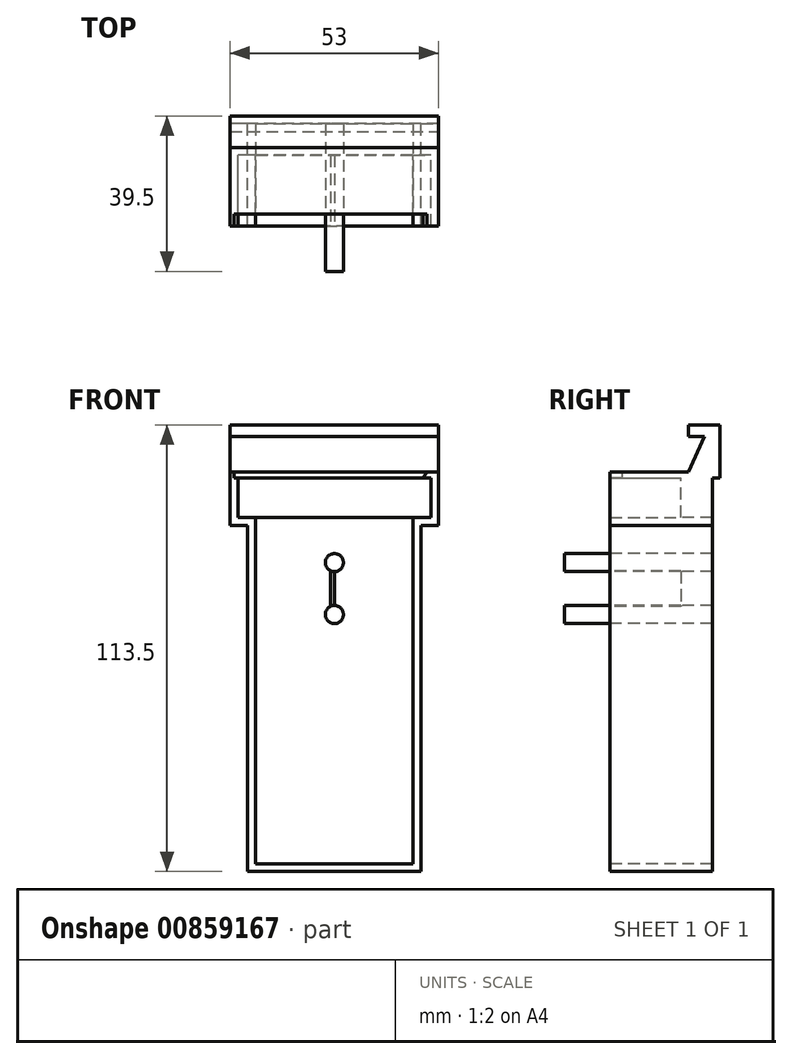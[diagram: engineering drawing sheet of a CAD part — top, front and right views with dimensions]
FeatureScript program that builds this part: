
annotation { "Feature Type Name" : "Feature", "Feature Type Description" : "" }
export const myFeature = defineFeature(function(context is Context, id is Id, definition is map)
    precondition{}
    {
        {
            var Q0;
            Q0=qCreatedBy(makeId("Front.planeOp"),FACE);
            var sketch = newSketch(context, id + "F0", { "sketchPlane" : qUnion([Q0])});
            skLineSegment(sketch, "E0.bottom", {"start": v(0, 0) * mm, "end": v(53, 0) * mm});
            skLineSegment(sketch, "E0.top", {"start": v(0, 3) * mm, "end": v(53, 3) * mm});
            skLineSegment(sketch, "E0.left", {"start": v(0, 0) * mm, "end": v(0, 3) * mm});
            skLineSegment(sketch, "E0.right", {"start": v(53, 0) * mm, "end": v(53, 3) * mm});
            skSolve(sketch);
        }
        {
            var Q0;
            Q0 = qSketchRegion(id + "F0", true);
            extrude(context, id + "F1", {"entities" : qUnion([Q0]), "depth" : 8 * mm, "offsetDistance" : 25 * mm});
        }
        {
            var Q0;
            Q0=makeQuery(id+"F1.opExtrude","SWEPT_FACE",FACE,{"disambiguationData":[OSD([sQuery(id+"F0.wireOp",EDGE,"E0.right")])]});
            var sketch = newSketch(context, id + "F2", { "sketchPlane" : qUnion([Q0])});
            skLineSegment(sketch, "E1", {"start": v(0, 0) * mm, "end": v(-4, 0) * mm});
            skLineSegment(sketch, "E2", {"start": v(0, 0) * mm, "end": v(0, -9) * mm});
            skLineSegment(sketch, "E3", {"start": v(0, -9) * mm, "end": v(-8, -9) * mm});
            skLineSegment(sketch, "E4", {"start": v(-8, -9) * mm, "end": v(-4, 0) * mm});
            skSolve(sketch);
        }
        {
            var Q0;
            Q0 = qSketchRegion(id + "F2", true);
            extrude(context, id + "F3", {"entities" : qUnion([Q0]), "operationType" : NewBodyOperationType.ADD, "depth" : -53 * mm, "offsetDistance" : 25 * mm});
        }
        {
            var Q0;
            Q0=makeQuery(id+"F1.opExtrude","CAP_FACE",FACE,{"disambiguationData":[OSD([sQuery(id+"F0.wireOp",EDGE,"E0.bottom"),sQuery(id+"F0.wireOp",EDGE,"E0.top"),sQuery(id+"F0.wireOp",EDGE,"E0.left"),sQuery(id+"F0.wireOp",EDGE,"E0.right")])],"isStart":false});
            var sketch = newSketch(context, id + "F4", { "sketchPlane" : qUnion([Q0])});
            skLineSegment(sketch, "E5", {"start": v(53, 3) * mm, "end": v(53, -9) * mm});
            skPoint(sketch, "E5.endSnap0", {"position": v(53, 1.5) * mm});
            skLineSegment(sketch, "E6.bottom", {"start": v(53, -9) * mm, "end": v(50, -9) * mm});
            skLineSegment(sketch, "E6.left", {"start": v(53, -9) * mm, "end": v(53, -10) * mm});
            skLineSegment(sketch, "E7", {"start": v(49.5, -9) * mm, "end": v(50, -9) * mm});
            skLineSegment(sketch, "E8", {"start": v(49.5, -9) * mm, "end": v(45, -9) * mm});
            skLineSegment(sketch, "E9", {"start": v(45, -9) * mm, "end": v(45, -10) * mm});
            skLineSegment(sketch, "E10", {"start": v(53, -9) * mm, "end": v(53, -10.5) * mm});
            skLineSegment(sketch, "E11", {"start": v(53, -10.5) * mm, "end": v(50, -10.5) * mm});
            skLineSegment(sketch, "E12", {"start": v(45, -10) * mm, "end": v(45, -10.5) * mm});
            skLineSegment(sketch, "E13", {"start": v(45, -10.5) * mm, "end": v(50, -10.5) * mm});
            skLineSegment(sketch, "E14", {"start": v(53, -10.5) * mm, "end": v(49, -10.5) * mm});
            skLineSegment(sketch, "E15", {"start": v(49, -10.5) * mm, "end": v(50, -9) * mm});
            skLineSegment(sketch, "E16", {"start": v(49.5, -9) * mm, "end": v(49.5, -9.75) * mm});
            skSolve(sketch);
        }
        {
            var Q0;
            Q0=makeQuery(id+"F4.imprint","IMPRINT",FACE,{"disambiguationData":[TD([[makeQuery(id+"F4.imprint","IMPRINT",EDGE,{"derivedFrom":sQuery(id+"F4.wireOp",EDGE,"t7llfW6A-werJ-ecjy-mYfy-ns4PyMyV4q1R")}),1.0]])]});
            var Q1;
            Q1=makeQuery(id+"F4.imprint","IMPRINT",FACE,{"disambiguationData":[TD([[makeQuery(id+"F4.imprint","IMPRINT",EDGE,{"derivedFrom":sQuery(id+"F4.wireOp",EDGE,"E6.right")}),-1.0]])]});
            var Q2;
            Q2=makeQuery(id+"F4.imprint","IMPRINT",FACE,{"disambiguationData":[TD([[makeQuery(id+"F4.imprint","IMPRINT",EDGE,{"derivedFrom":sQuery(id+"F4.wireOp",EDGE,"E6.bottom")}),1.0]])]});
            extrude(context, id + "F5", {"entities" : qUnion([Q0, Q1, Q2]), "operationType" : NewBodyOperationType.ADD, "depth" : -8 * mm, "offsetDistance" : 25 * mm});
        }
        {
            var Q0;
            Q0=makeQuery(id+"F4.imprint","IMPRINT",FACE,{"disambiguationData":[TD([[makeQuery(id+"F4.imprint","IMPRINT",EDGE,{"derivedFrom":sQuery(id+"F4.wireOp",EDGE,"E6.bottom")}),1.0]])]});
            var Q1;
            Q1=makeQuery(id+"F4.imprint","IMPRINT",FACE,{"disambiguationData":[TD([[makeQuery(id+"F4.imprint","IMPRINT",EDGE,{"derivedFrom":sQuery(id+"F4.wireOp",EDGE,"E6.right")}),-1.0]])]});
            var Q2;
            Q2=makeQuery(id+"F4.imprint","IMPRINT",FACE,{"disambiguationData":[TD([[makeQuery(id+"F4.imprint","IMPRINT",EDGE,{"derivedFrom":sQuery(id+"F4.wireOp",EDGE,"t7llfW6A-werJ-ecjy-mYfy-ns4PyMyV4q1R")}),1.0]])]});
            extrude(context, id + "F6", {"entities" : qUnion([Q0, Q1, Q2]), "operationType" : NewBodyOperationType.ADD, "depth" : 17 * mm, "offsetDistance" : 25 * mm});
        }
        {
            var Q0;
            Q0=makeQuery(id+"F4.imprint","IMPRINT",FACE,{"disambiguationData":[TD([[makeQuery(id+"F4.imprint","IMPRINT",EDGE,{"derivedFrom":sQuery(id+"F4.wireOp",EDGE,"E6.right")}),-1.0]])]});
            var Q1;
            Q1=makeQuery(id+"F4.imprint","IMPRINT",FACE,{"disambiguationData":[TD([[makeQuery(id+"F4.imprint","IMPRINT",EDGE,{"derivedFrom":sQuery(id+"F4.wireOp",EDGE,"E6.bottom")}),1.0]])]});
            extrude(context, id + "F7", {"entities" : qUnion([Q0, Q1]), "operationType" : NewBodyOperationType.ADD, "depth" : 20 * mm, "offsetDistance" : 25 * mm});
        }
        {
            var Q0;
            Q0=makeQuery(id+"F1.opExtrude","CAP_FACE",FACE,{"disambiguationData":[OSD([sQuery(id+"F0.wireOp",EDGE,"E0.bottom"),sQuery(id+"F0.wireOp",EDGE,"E0.top"),sQuery(id+"F0.wireOp",EDGE,"E0.left"),sQuery(id+"F0.wireOp",EDGE,"E0.right")])],"isStart":false});
            var sketch = newSketch(context, id + "F8", { "sketchPlane" : qUnion([Q0])});
            skLineSegment(sketch, "E17", {"start": v(0, 3) * mm, "end": v(0, -9) * mm});
            skLineSegment(sketch, "E18.bottom", {"start": v(0, -9) * mm, "end": v(1, -9) * mm});
            skLineSegment(sketch, "E18.top", {"start": v(0, -10.5) * mm, "end": v(1, -10.5) * mm});
            skLineSegment(sketch, "E18.left", {"start": v(0, -9) * mm, "end": v(0, -10.5) * mm});
            skLineSegment(sketch, "E18.right", {"start": v(1, -9) * mm, "end": v(1, -10.5) * mm});
            skLineSegment(sketch, "E19.bottom", {"start": v(1, -10.5) * mm, "end": v(8, -10.5) * mm});
            skLineSegment(sketch, "E19.top", {"start": v(1, -9) * mm, "end": v(8, -9) * mm});
            skLineSegment(sketch, "E19.left", {"start": v(1, -10.5) * mm, "end": v(1, -9) * mm});
            skLineSegment(sketch, "E20", {"start": v(8, -9) * mm, "end": v(49.5, -9) * mm});
            skLineSegment(sketch, "E21", {"start": v(8, -10.5) * mm, "end": v(49.5, -10.5) * mm});
            skLineSegment(sketch, "E22", {"start": v(49.5, -10.5) * mm, "end": v(49.5, -9) * mm});
            skSolve(sketch);
        }
        {
            var Q0;
            Q0=makeQuery(id+"F8.imprint","IMPRINT",FACE,{"disambiguationData":[TD([[makeQuery(id+"F8.imprint","IMPRINT",EDGE,{"derivedFrom":sQuery(id+"F8.wireOp",EDGE,"E18.bottom")}),-1.0]])]});
            var Q1;
            Q1=makeQuery(id+"F8.imprint","IMPRINT",FACE,{"disambiguationData":[TD([[makeQuery(id+"F8.imprint","IMPRINT",EDGE,{"derivedFrom":sQuery(id+"F8.wireOp",EDGE,"E19.bottom")}),1.0]])]});
            extrude(context, id + "F9", {"entities" : qUnion([Q0, Q1]), "operationType" : NewBodyOperationType.ADD, "depth" : -8 * mm, "offsetDistance" : 25 * mm});
        }
        {
            var Q0;
            Q0=makeQuery(id+"F8.imprint","IMPRINT",FACE,{"disambiguationData":[TD([[makeQuery(id+"F8.imprint","IMPRINT",EDGE,{"derivedFrom":sQuery(id+"F8.wireOp",EDGE,"E18.bottom")}),-1.0]])]});
            extrude(context, id + "F10", {"entities" : qUnion([Q0]), "operationType" : NewBodyOperationType.ADD, "depth" : 20 * mm, "offsetDistance" : 25 * mm});
        }
        {
            var Q0;
            Q0=makeQuery(id+"F8.imprint","IMPRINT",FACE,{"disambiguationData":[TD([[makeQuery(id+"F8.imprint","IMPRINT",EDGE,{"derivedFrom":sQuery(id+"F8.wireOp",EDGE,"E19.bottom")}),1.0]])]});
            extrude(context, id + "F11", {"entities" : qUnion([Q0]), "operationType" : NewBodyOperationType.ADD, "depth" : 17 * mm, "offsetDistance" : 25 * mm});
        }
        {
            var Q0;
            {var subQ0=sQuery(id+"F8.wireOp",EDGE,"E21");var subQ1=sQuery(id+"F8.wireOp",EDGE,"E19.bottom");var subQ2=sQuery(id+"F8.wireOp",EDGE,"E18.top");var subQ3=sQuery(id+"F4.wireOp",EDGE,"E13");var subQ4=sQuery(id+"F4.wireOp",EDGE,"E11");Q0=makeQuery(id+"F11.boolean.opBoolean","MERGE",FACE,{"derivedFrom":[makeQuery(id+"F10.boolean.opBoolean","MERGE",FACE,{"derivedFrom":[makeQuery(id+"F9.boolean.opBoolean","MERGE",FACE,{"derivedFrom":[makeQuery(id+"F7.boolean.opBoolean","MERGE",FACE,{"derivedFrom":[makeQuery(id+"F6.boolean.opBoolean","MERGE",FACE,{"derivedFrom":[makeQuery(id+"F5.opExtrude","SWEPT_FACE",FACE,{"disambiguationData":[OSD([subQ4,subQ3])]}),makeQuery(id+"F6.opExtrude","SWEPT_FACE",FACE,{"disambiguationData":[OSD([subQ4,subQ3])]})]}),makeQuery(id+"F7.opExtrude","SWEPT_FACE",FACE,{"disambiguationData":[OSD([subQ4,subQ3])]})]}),makeQuery(id+"F9.opExtrude","SWEPT_FACE",FACE,{"disambiguationData":[OSD([subQ2,subQ1,subQ0])]})]}),makeQuery(id+"F10.opExtrude","SWEPT_FACE",FACE,{"disambiguationData":[OSD([subQ2])]})]}),makeQuery(id+"F11.opExtrude","SWEPT_FACE",FACE,{"disambiguationData":[OSD([subQ1,subQ0])]})]});}
            var sketch = newSketch(context, id + "F12", { "sketchPlane" : qUnion([Q0])});
            skLineSegment(sketch, "E23.bottom", {"start": v(53, 28) * mm, "end": v(51, 28) * mm});
            skLineSegment(sketch, "E23.top", {"start": v(53, 15) * mm, "end": v(51, 15) * mm});
            skLineSegment(sketch, "E23.left", {"start": v(53, 28) * mm, "end": v(53, 15) * mm});
            skLineSegment(sketch, "E23.right", {"start": v(51, 28) * mm, "end": v(51, 15) * mm});
            skSolve(sketch);
        }
        {
            var Q0;
            Q0 = qSketchRegion(id + "F12", true);
            extrude(context, id + "F13", {"entities" : qUnion([Q0]), "operationType" : NewBodyOperationType.ADD, "depth" : 12 * mm, "offsetDistance" : 25 * mm});
        }
        {
            var Q0;
            Q0=makeQuery(id+"F13.opExtrude","SWEPT_FACE",FACE,{"disambiguationData":[OSD([sQuery(id+"F12.wireOp",EDGE,"E23.right")])]});
            var sketch = newSketch(context, id + "F14", { "sketchPlane" : qUnion([Q0])});
            skLineSegment(sketch, "E24.bottom", {"start": v(28, -22.5) * mm, "end": v(10, -22.5) * mm});
            skLineSegment(sketch, "E24.top", {"start": v(28, -20.5) * mm, "end": v(10, -20.5) * mm});
            skLineSegment(sketch, "E24.left", {"start": v(28, -22.5) * mm, "end": v(28, -20.5) * mm});
            skLineSegment(sketch, "E24.right", {"start": v(10, -22.5) * mm, "end": v(10, -20.5) * mm});
            skSolve(sketch);
        }
        {
            var Q0;
            Q0 = qSketchRegion(id + "F14", true);
            extrude(context, id + "F15", {"entities" : qUnion([Q0]), "operationType" : NewBodyOperationType.ADD, "depth" : 2.5 * mm, "offsetDistance" : 25 * mm});
        }
        {
            var Q0;
            {var subQ0=sQuery(id+"F4.wireOp",EDGE,"E7");Q0=makeQuery(id+"F4.imprint","IMPRINT",FACE,{"disambiguationData":[TD([[makeQuery(id+"F4.imprint","IMPRINT",EDGE,{"derivedFrom":subQ0}),-1.0]])]});}
            extrude(context, id + "F16", {"entities" : qUnion([Q0]), "operationType" : NewBodyOperationType.ADD, "depth" : -8 * mm, "offsetDistance" : 25 * mm});
        }
        {
            var Q0;
            {var subQ0=sQuery(id+"F4.wireOp",EDGE,"E7");Q0=makeQuery(id+"F4.imprint","IMPRINT",FACE,{"disambiguationData":[TD([[makeQuery(id+"F4.imprint","IMPRINT",EDGE,{"derivedFrom":subQ0}),-1.0]])]});}
            extrude(context, id + "F17", {"entities" : qUnion([Q0]), "operationType" : NewBodyOperationType.ADD, "depth" : 17 * mm, "offsetDistance" : 25 * mm});
        }
        {
            var Q0;
            Q0=makeQuery(id+"F15.boolean.opBoolean","MERGE",FACE,{"derivedFrom":[makeQuery(id+"F13.opExtrude","CAP_FACE",FACE,{"disambiguationData":[OSD([sQuery(id+"F12.wireOp",EDGE,"E23.bottom"),sQuery(id+"F12.wireOp",EDGE,"E23.top"),sQuery(id+"F12.wireOp",EDGE,"E23.left"),sQuery(id+"F12.wireOp",EDGE,"E23.right")])],"isStart":false}),makeQuery(id+"F15.opExtrude","SWEPT_FACE",FACE,{"disambiguationData":[OSD([sQuery(id+"F14.wireOp",EDGE,"E24.bottom")])]})]});
            var sketch = newSketch(context, id + "F18", { "sketchPlane" : qUnion([Q0])});
            skLineSegment(sketch, "E25.bottom", {"start": v(48.5, 28) * mm, "end": v(46.5, 28) * mm});
            skLineSegment(sketch, "E25.top", {"start": v(48.5, 10) * mm, "end": v(46.5, 10) * mm});
            skLineSegment(sketch, "E25.left", {"start": v(48.5, 28) * mm, "end": v(48.5, 10) * mm});
            skLineSegment(sketch, "E25.right", {"start": v(46.5, 28) * mm, "end": v(46.5, 10) * mm});
            skSolve(sketch);
        }
        {
            var Q0;
            Q0 = qSketchRegion(id + "F18", true);
            extrude(context, id + "F19", {"entities" : qUnion([Q0]), "operationType" : NewBodyOperationType.ADD, "depth" : -2 * mm, "offsetDistance" : 25 * mm});
        }
        {
            var Q0;
            Q0 = qSketchRegion(id + "F18", true);
            extrude(context, id + "F20", {"entities" : qUnion([Q0]), "operationType" : NewBodyOperationType.ADD, "depth" : 88 * mm, "offsetDistance" : 25 * mm});
        }
        {
            var Q0;
            {var subQ0=sQuery(id+"F8.wireOp",EDGE,"E21");var subQ1=sQuery(id+"F8.wireOp",EDGE,"E19.bottom");var subQ2=sQuery(id+"F8.wireOp",EDGE,"E18.top");var subQ3=sQuery(id+"F4.wireOp",EDGE,"E14");Q0=makeQuery(id+"F11.boolean.opBoolean","MERGE",FACE,{"derivedFrom":[makeQuery(id+"F10.boolean.opBoolean","MERGE",FACE,{"derivedFrom":[makeQuery(id+"F9.boolean.opBoolean","MERGE",FACE,{"derivedFrom":[makeQuery(id+"F7.boolean.opBoolean","MERGE",FACE,{"derivedFrom":[makeQuery(id+"F6.boolean.opBoolean","MERGE",FACE,{"derivedFrom":[makeQuery(id+"F5.opExtrude","SWEPT_FACE",FACE,{"disambiguationData":[OSD([subQ3])]}),makeQuery(id+"F6.opExtrude","SWEPT_FACE",FACE,{"disambiguationData":[OSD([subQ3])]})]}),makeQuery(id+"F7.opExtrude","SWEPT_FACE",FACE,{"disambiguationData":[OSD([subQ3])]})]}),makeQuery(id+"F9.opExtrude","SWEPT_FACE",FACE,{"disambiguationData":[OSD([subQ2,subQ1,subQ0])]})]}),makeQuery(id+"F10.opExtrude","SWEPT_FACE",FACE,{"disambiguationData":[OSD([subQ2])]})]}),makeQuery(id+"F11.opExtrude","SWEPT_FACE",FACE,{"disambiguationData":[OSD([subQ1,subQ0])]})]});}
            var sketch = newSketch(context, id + "F21", { "sketchPlane" : qUnion([Q0])});
            skLineSegment(sketch, "E26.bottom", {"start": v(0, 28) * mm, "end": v(2, 28) * mm});
            skLineSegment(sketch, "E26.top", {"start": v(0, 15) * mm, "end": v(2, 15) * mm});
            skLineSegment(sketch, "E26.left", {"start": v(0, 28) * mm, "end": v(0, 15) * mm});
            skLineSegment(sketch, "E26.right", {"start": v(2, 28) * mm, "end": v(2, 15) * mm});
            skSolve(sketch);
        }
        {
            var Q0;
            Q0 = qSketchRegion(id + "F21", true);
            extrude(context, id + "F22", {"entities" : qUnion([Q0]), "operationType" : NewBodyOperationType.ADD, "depth" : 12 * mm, "offsetDistance" : 25 * mm});
        }
        {
            var Q0;
            Q0=makeQuery(id+"F22.opExtrude","SWEPT_FACE",FACE,{"disambiguationData":[OSD([sQuery(id+"F21.wireOp",EDGE,"E26.right")])]});
            var sketch = newSketch(context, id + "F23", { "sketchPlane" : qUnion([Q0])});
            skLineSegment(sketch, "E27.bottom", {"start": v(-28, -22.5) * mm, "end": v(-10, -22.5) * mm});
            skLineSegment(sketch, "E27.top", {"start": v(-28, -20.5) * mm, "end": v(-10, -20.5) * mm});
            skLineSegment(sketch, "E27.left", {"start": v(-28, -22.5) * mm, "end": v(-28, -20.5) * mm});
            skLineSegment(sketch, "E27.right", {"start": v(-10, -22.5) * mm, "end": v(-10, -20.5) * mm});
            skSolve(sketch);
        }
        {
            var Q0;
            Q0 = qSketchRegion(id + "F23", true);
            extrude(context, id + "F24", {"entities" : qUnion([Q0]), "operationType" : NewBodyOperationType.ADD, "depth" : 4.5 * mm, "offsetDistance" : 25 * mm});
        }
        {
            var Q0;
            Q0=makeQuery(id+"F24.boolean.opBoolean","MERGE",FACE,{"derivedFrom":[makeQuery(id+"F22.opExtrude","CAP_FACE",FACE,{"disambiguationData":[OSD([sQuery(id+"F21.wireOp",EDGE,"E26.bottom"),sQuery(id+"F21.wireOp",EDGE,"E26.top"),sQuery(id+"F21.wireOp",EDGE,"E26.left"),sQuery(id+"F21.wireOp",EDGE,"E26.right")])],"isStart":false}),makeQuery(id+"F24.opExtrude","SWEPT_FACE",FACE,{"disambiguationData":[OSD([sQuery(id+"F23.wireOp",EDGE,"E27.bottom")])]})]});
            var sketch = newSketch(context, id + "F25", { "sketchPlane" : qUnion([Q0])});
            skLineSegment(sketch, "E28.bottom", {"start": v(6.5, 28) * mm, "end": v(4.5, 28) * mm});
            skLineSegment(sketch, "E28.top", {"start": v(6.5, 10) * mm, "end": v(4.5, 10) * mm});
            skLineSegment(sketch, "E28.left", {"start": v(6.5, 28) * mm, "end": v(6.5, 10) * mm});
            skLineSegment(sketch, "E28.right", {"start": v(4.5, 28) * mm, "end": v(4.5, 10) * mm});
            skSolve(sketch);
        }
        {
            var Q0;
            Q0 = qSketchRegion(id + "F25", true);
            extrude(context, id + "F26", {"entities" : qUnion([Q0]), "operationType" : NewBodyOperationType.ADD, "depth" : 88 * mm, "offsetDistance" : 25 * mm});
        }
        {
            var Q0;
            Q0=makeQuery(id+"F22.opExtrude","SWEPT_FACE",FACE,{"disambiguationData":[OSD([sQuery(id+"F21.wireOp",EDGE,"E26.top")])]});
            var sketch = newSketch(context, id + "F27", { "sketchPlane" : qUnion([Q0])});
            skLineSegment(sketch, "E29.bottom", {"start": v(0, -10.5) * mm, "end": v(-2, -10.5) * mm});
            skLineSegment(sketch, "E29.top", {"start": v(0, -22.5) * mm, "end": v(-2, -22.5) * mm});
            skLineSegment(sketch, "E29.left", {"start": v(0, -10.5) * mm, "end": v(0, -22.5) * mm});
            skLineSegment(sketch, "E29.right", {"start": v(-2, -10.5) * mm, "end": v(-2, -22.5) * mm});
            skSolve(sketch);
        }
        {
            var Q0;
            Q0 = qSketchRegion(id + "F27", true);
            extrude(context, id + "F28", {"entities" : qUnion([Q0]), "operationType" : NewBodyOperationType.ADD, "depth" : 5 * mm, "offsetDistance" : 25 * mm});
        }
        {
            var Q0;
            Q0=makeQuery(id+"F13.opExtrude","SWEPT_FACE",FACE,{"disambiguationData":[OSD([sQuery(id+"F12.wireOp",EDGE,"E23.top")])]});
            var sketch = newSketch(context, id + "F29", { "sketchPlane" : qUnion([Q0])});
            skLineSegment(sketch, "E30.bottom", {"start": v(-51, -10.5) * mm, "end": v(-53, -10.5) * mm});
            skLineSegment(sketch, "E30.top", {"start": v(-51, -22.5) * mm, "end": v(-53, -22.5) * mm});
            skLineSegment(sketch, "E30.left", {"start": v(-51, -10.5) * mm, "end": v(-51, -22.5) * mm});
            skLineSegment(sketch, "E30.right", {"start": v(-53, -10.5) * mm, "end": v(-53, -22.5) * mm});
            skSolve(sketch);
        }
        {
            var Q0;
            Q0 = qSketchRegion(id + "F29", true);
            extrude(context, id + "F30", {"entities" : qUnion([Q0]), "operationType" : NewBodyOperationType.ADD, "depth" : 5 * mm, "offsetDistance" : 25 * mm});
        }
        {
            var Q0;
            Q0=makeQuery(id+"F28.boolean.opBoolean","MERGE",FACE,{"derivedFrom":[makeQuery(id+"F26.boolean.opBoolean","MERGE",FACE,{"derivedFrom":[makeQuery(id+"F24.opExtrude","SWEPT_FACE",FACE,{"disambiguationData":[OSD([sQuery(id+"F23.wireOp",EDGE,"E27.right")])]}),makeQuery(id+"F26.opExtrude","SWEPT_FACE",FACE,{"disambiguationData":[OSD([sQuery(id+"F25.wireOp",EDGE,"E28.top")])]})]}),makeQuery(id+"F28.opExtrude","CAP_FACE",FACE,{"disambiguationData":[OSD([sQuery(id+"F27.wireOp",EDGE,"E29.bottom"),sQuery(id+"F27.wireOp",EDGE,"E29.top"),sQuery(id+"F27.wireOp",EDGE,"E29.left"),sQuery(id+"F27.wireOp",EDGE,"E29.right")])],"isStart":false})]});
            var sketch = newSketch(context, id + "F31", { "sketchPlane" : qUnion([Q0])});
            skLineSegment(sketch, "E31.bottom", {"start": v(-2, -10.5) * mm, "end": v(-51, -10.5) * mm});
            skLineSegment(sketch, "E31.top", {"start": v(-2, -20.5) * mm, "end": v(-51, -20.5) * mm});
            skLineSegment(sketch, "E31.left", {"start": v(-2, -10.5) * mm, "end": v(-2, -20.5) * mm});
            skLineSegment(sketch, "E31.right", {"start": v(-51, -10.5) * mm, "end": v(-51, -20.5) * mm});
            skLineSegment(sketch, "E32.bottom", {"start": v(-6.5, -20.5) * mm, "end": v(-46.5, -20.5) * mm});
            skLineSegment(sketch, "E32.top", {"start": v(-6.5, -108.5) * mm, "end": v(-46.5, -108.5) * mm});
            skLineSegment(sketch, "E32.left", {"start": v(-6.5, -20.5) * mm, "end": v(-6.5, -108.5) * mm});
            skLineSegment(sketch, "E32.right", {"start": v(-46.5, -20.5) * mm, "end": v(-46.5, -108.5) * mm});
            skLineSegment(sketch, "E33.top", {"start": v(-6.5, -110.5) * mm, "end": v(-46.5, -110.5) * mm});
            skLineSegment(sketch, "E33.left", {"start": v(-6.5, -108.5) * mm, "end": v(-6.5, -110.5) * mm});
            skLineSegment(sketch, "E33.right", {"start": v(-46.5, -108.5) * mm, "end": v(-46.5, -110.5) * mm});
            skSolve(sketch);
        }
        {
            var Q0;
            {var subQ0=sQuery(id+"F31.wireOp",EDGE,"E31.left");Q0=makeQuery(id+"F31.imprint","IMPRINT",FACE,{"disambiguationData":[TD([[makeQuery(id+"F31.imprint","IMPRINT",EDGE,{"derivedFrom":subQ0}),-1.0]])]});}
            var Q1;
            {var subQ0=sQuery(id+"F18.wireOp",EDGE,"E25.top");Q1=makeQuery(id+"F30.boolean.opBoolean","MERGE",FACE,{"derivedFrom":[makeQuery(id+"F20.boolean.opBoolean","MERGE",FACE,{"derivedFrom":[makeQuery(id+"F19.boolean.opBoolean","MERGE",FACE,{"derivedFrom":[makeQuery(id+"F15.opExtrude","SWEPT_FACE",FACE,{"disambiguationData":[OSD([sQuery(id+"F14.wireOp",EDGE,"E24.right")])]}),makeQuery(id+"F19.opExtrude","SWEPT_FACE",FACE,{"disambiguationData":[OSD([subQ0])]})]}),makeQuery(id+"F20.opExtrude","SWEPT_FACE",FACE,{"disambiguationData":[OSD([subQ0])]})]}),makeQuery(id+"F30.opExtrude","CAP_FACE",FACE,{"disambiguationData":[OSD([sQuery(id+"F29.wireOp",EDGE,"E30.bottom"),sQuery(id+"F29.wireOp",EDGE,"E30.top"),sQuery(id+"F29.wireOp",EDGE,"E30.left"),sQuery(id+"F29.wireOp",EDGE,"E30.right")])],"isStart":false})]});}
            var Q2;
            Q2=makeQuery(id+"F31.imprint","IMPRINT",FACE,{"disambiguationData":[TD([[makeQuery(id+"F31.imprint","IMPRINT",EDGE,{"derivedFrom":sQuery(id+"F31.wireOp",EDGE,"E31.bottom")}),1.0]])]});
            var Q3;
            Q3=makeQuery(id+"F31.imprint","IMPRINT",FACE,{"disambiguationData":[TD([[makeQuery(id+"F31.imprint","IMPRINT",EDGE,{"derivedFrom":sQuery(id+"F31.wireOp",EDGE,"E32.bottom")}),1.0]])]});
            var Q4;
            Q4=makeQuery(id+"F31.imprint","IMPRINT",FACE,{"disambiguationData":[TD([[makeQuery(id+"F31.imprint","IMPRINT",EDGE,{"derivedFrom":sQuery(id+"F31.wireOp",EDGE,"E32.top")}),1.0]])]});
            extrude(context, id + "F32", {"entities" : qUnion([Q0, Q1, Q2, Q3, Q4]), "operationType" : NewBodyOperationType.ADD, "depth" : 8 * mm, "offsetDistance" : 25 * mm});
        }
        {
            var Q0;
            Q0=makeQuery(id+"F26.boolean.opBoolean","MERGE",FACE,{"derivedFrom":[makeQuery(id+"F24.boolean.opBoolean","MERGE",FACE,{"derivedFrom":[makeQuery(id+"F22.boolean.opBoolean","MERGE",FACE,{"derivedFrom":[makeQuery(id+"F10.opExtrude","CAP_FACE",FACE,{"disambiguationData":[OSD([sQuery(id+"F8.wireOp",EDGE,"E18.bottom"),sQuery(id+"F8.wireOp",EDGE,"E18.top"),sQuery(id+"F8.wireOp",EDGE,"E18.left"),sQuery(id+"F8.wireOp",EDGE,"E19.left")])],"isStart":false}),makeQuery(id+"F22.opExtrude","SWEPT_FACE",FACE,{"disambiguationData":[OSD([sQuery(id+"F21.wireOp",EDGE,"E26.bottom")])]})]}),makeQuery(id+"F24.opExtrude","SWEPT_FACE",FACE,{"disambiguationData":[OSD([sQuery(id+"F23.wireOp",EDGE,"E27.left")])]})]}),makeQuery(id+"F26.opExtrude","SWEPT_FACE",FACE,{"disambiguationData":[OSD([sQuery(id+"F25.wireOp",EDGE,"E28.bottom")])]})]});
            var sketch = newSketch(context, id + "F33", { "sketchPlane" : qUnion([Q0])});
            skLineSegment(sketch, "E34", {"start": v(6.5, -20.5) * mm, "end": v(46.5, -20.5) * mm});
            skLineSegment(sketch, "E35", {"start": v(26.5, -20.5) * mm, "end": v(26.5, -47.5) * mm});
            skLineSegment(sketch, "E36", {"start": v(26.5, -47.5) * mm, "end": v(26.5, -42.9) * mm});
            skCircle(sketch, "E37", {"center": v(26.5, -45.2) * mm, "radius": 2.3 * mm});
            skLineSegment(sketch, "E38", {"start": v(26.5, -42.9) * mm, "end": v(26.5, -34.3) * mm});
            skLineSegment(sketch, "E39", {"start": v(26.5, -34.3) * mm, "end": v(26.5, -29.7) * mm});
            skCircle(sketch, "E40", {"center": v(26.5, -32) * mm, "radius": 2.3 * mm});
            skLineSegment(sketch, "E41", {"start": v(26.5, -29.7) * mm, "end": v(26.5, -20.5) * mm});
            skLineSegment(sketch, "E42.bottom", {"start": v(26.5, -20.5) * mm, "end": v(27.5, -20.5) * mm});
            skLineSegment(sketch, "E42.top", {"start": v(26.5, -47.5) * mm, "end": v(27.5, -47.5) * mm});
            skLineSegment(sketch, "E42.right", {"start": v(27.5, -20.5) * mm, "end": v(27.5, -47.5) * mm});
            skLineSegment(sketch, "E43.bottom", {"start": v(26.5, -20.5) * mm, "end": v(25.5, -20.5) * mm});
            skLineSegment(sketch, "E43.top", {"start": v(26.5, -47.5) * mm, "end": v(25.5, -47.5) * mm});
            skLineSegment(sketch, "E43.right", {"start": v(25.5, -20.5) * mm, "end": v(25.5, -47.5) * mm});
            skSolve(sketch);
        }
        {
            var Q0;
            {var subQ0=sQuery(id+"F33.wireOp",EDGE,"E43.right");var subQ1=sQuery(id+"F33.wireOp",EDGE,"E37");var subQ2=makeQuery(id+"F33.imprint","INTERSECT",VERTEX,{"disambiguationData":[OD(0.0)],"derivedFrom":[subQ1,subQ0]});Q0=makeQuery(id+"F33.imprint","IMPRINT",FACE,{"disambiguationData":[TD([[makeQuery(id+"F33.imprint","IMPRINT",EDGE,{"disambiguationData":[TD([[subQ2,1.0]])],"derivedFrom":subQ1}),1.0]])]});}
            var Q1;
            {var subQ0=sQuery(id+"F33.wireOp",EDGE,"E42.right");var subQ1=sQuery(id+"F33.wireOp",EDGE,"E37");var subQ2=makeQuery(id+"F33.imprint","INTERSECT",VERTEX,{"disambiguationData":[OD(0.0)],"derivedFrom":[subQ1,subQ0]});Q1=makeQuery(id+"F33.imprint","IMPRINT",FACE,{"disambiguationData":[TD([[makeQuery(id+"F33.imprint","IMPRINT",EDGE,{"disambiguationData":[TD([[subQ2,-1.0]])],"derivedFrom":subQ1}),1.0]])]});}
            var Q2;
            {var subQ0=sQuery(id+"F33.wireOp",EDGE,"E42.right");var subQ1=sQuery(id+"F33.wireOp",EDGE,"E37");var subQ2=makeQuery(id+"F33.imprint","INTERSECT",VERTEX,{"disambiguationData":[OD(0.0)],"derivedFrom":[subQ1,subQ0]});Q2=makeQuery(id+"F33.imprint","IMPRINT",FACE,{"disambiguationData":[TD([[makeQuery(id+"F33.imprint","IMPRINT",EDGE,{"disambiguationData":[TD([[subQ2,-1.0]])],"derivedFrom":subQ1}),-1.0]])]});}
            var Q3;
            {var subQ0=sQuery(id+"F33.wireOp",EDGE,"E43.right");var subQ1=sQuery(id+"F33.wireOp",EDGE,"E37");var subQ2=makeQuery(id+"F33.imprint","INTERSECT",VERTEX,{"disambiguationData":[OD(0.0)],"derivedFrom":[subQ1,subQ0]});Q3=makeQuery(id+"F33.imprint","IMPRINT",FACE,{"disambiguationData":[TD([[makeQuery(id+"F33.imprint","IMPRINT",EDGE,{"disambiguationData":[TD([[subQ2,1.0]])],"derivedFrom":subQ1}),-1.0]])]});}
            var Q4;
            {var subQ0=sQuery(id+"F33.wireOp",EDGE,"E43.right");var subQ1=sQuery(id+"F33.wireOp",EDGE,"E40");var subQ2=makeQuery(id+"F33.imprint","INTERSECT",VERTEX,{"disambiguationData":[OD(0.0)],"derivedFrom":[subQ1,subQ0]});Q4=makeQuery(id+"F33.imprint","IMPRINT",FACE,{"disambiguationData":[TD([[makeQuery(id+"F33.imprint","IMPRINT",EDGE,{"disambiguationData":[TD([[subQ2,1.0]])],"derivedFrom":subQ1}),1.0]])]});}
            var Q5;
            {var subQ0=sQuery(id+"F33.wireOp",EDGE,"E42.right");var subQ1=sQuery(id+"F33.wireOp",EDGE,"E40");var subQ2=makeQuery(id+"F33.imprint","INTERSECT",VERTEX,{"disambiguationData":[OD(0.0)],"derivedFrom":[subQ1,subQ0]});Q5=makeQuery(id+"F33.imprint","IMPRINT",FACE,{"disambiguationData":[TD([[makeQuery(id+"F33.imprint","IMPRINT",EDGE,{"disambiguationData":[TD([[subQ2,-1.0]])],"derivedFrom":subQ1}),1.0]])]});}
            var Q6;
            {var subQ5=sQuery(id+"F33.wireOp",EDGE,"E42.bottom");Q6=makeQuery(id+"F33.imprint","IMPRINT",FACE,{"disambiguationData":[TD([[makeQuery(id+"F33.imprint","IMPRINT",EDGE,{"derivedFrom":subQ5}),-1.0]])]});}
            var Q7;
            {var subQ5=sQuery(id+"F33.wireOp",EDGE,"E43.bottom");Q7=makeQuery(id+"F33.imprint","IMPRINT",FACE,{"disambiguationData":[TD([[makeQuery(id+"F33.imprint","IMPRINT",EDGE,{"derivedFrom":subQ5}),1.0]])]});}
            extrude(context, id + "F34", {"entities" : qUnion([Q0, Q1, Q2, Q3, Q4, Q5, Q6, Q7]), "operationType" : NewBodyOperationType.ADD, "depth" : -18 * mm, "offsetDistance" : 25 * mm});
        }
        {
            var Q0;
            {var subQ0=sQuery(id+"F33.wireOp",EDGE,"E42.right");var subQ1=sQuery(id+"F33.wireOp",EDGE,"E40");var subQ2=makeQuery(id+"F33.imprint","INTERSECT",VERTEX,{"disambiguationData":[OD(0.0)],"derivedFrom":[subQ1,subQ0]});Q0=makeQuery(id+"F33.imprint","IMPRINT",FACE,{"disambiguationData":[TD([[makeQuery(id+"F33.imprint","IMPRINT",EDGE,{"disambiguationData":[TD([[subQ2,1.0]])],"derivedFrom":subQ1}),1.0]])]});}
            var Q1;
            {var subQ0=sQuery(id+"F33.wireOp",EDGE,"E42.right");var subQ1=sQuery(id+"F33.wireOp",EDGE,"E40");var subQ2=makeQuery(id+"F33.imprint","INTERSECT",VERTEX,{"disambiguationData":[OD(0.0)],"derivedFrom":[subQ1,subQ0]});Q1=makeQuery(id+"F33.imprint","IMPRINT",FACE,{"disambiguationData":[TD([[makeQuery(id+"F33.imprint","IMPRINT",EDGE,{"disambiguationData":[TD([[subQ2,-1.0]])],"derivedFrom":subQ1}),1.0]])]});}
            var Q2;
            {var subQ0=sQuery(id+"F33.wireOp",EDGE,"E43.right");var subQ1=sQuery(id+"F33.wireOp",EDGE,"E40");var subQ2=makeQuery(id+"F33.imprint","INTERSECT",VERTEX,{"disambiguationData":[OD(0.0)],"derivedFrom":[subQ1,subQ0]});Q2=makeQuery(id+"F33.imprint","IMPRINT",FACE,{"disambiguationData":[TD([[makeQuery(id+"F33.imprint","IMPRINT",EDGE,{"disambiguationData":[TD([[subQ2,1.0]])],"derivedFrom":subQ1}),1.0]])]});}
            var Q3;
            {var subQ0=sQuery(id+"F33.wireOp",EDGE,"E43.right");var subQ1=sQuery(id+"F33.wireOp",EDGE,"E40");var subQ2=makeQuery(id+"F33.imprint","INTERSECT",VERTEX,{"disambiguationData":[OD(0.0)],"derivedFrom":[subQ1,subQ0]});Q3=makeQuery(id+"F33.imprint","IMPRINT",FACE,{"disambiguationData":[TD([[makeQuery(id+"F33.imprint","IMPRINT",EDGE,{"disambiguationData":[TD([[subQ2,-1.0]])],"derivedFrom":subQ1}),1.0]])]});}
            var Q4;
            {var subQ0=sQuery(id+"F33.wireOp",EDGE,"E43.right");var subQ1=sQuery(id+"F33.wireOp",EDGE,"E37");var subQ2=makeQuery(id+"F33.imprint","INTERSECT",VERTEX,{"disambiguationData":[OD(0.0)],"derivedFrom":[subQ1,subQ0]});Q4=makeQuery(id+"F33.imprint","IMPRINT",FACE,{"disambiguationData":[TD([[makeQuery(id+"F33.imprint","IMPRINT",EDGE,{"disambiguationData":[TD([[subQ2,1.0]])],"derivedFrom":subQ1}),1.0]])]});}
            var Q5;
            {var subQ0=sQuery(id+"F33.wireOp",EDGE,"E43.right");var subQ1=sQuery(id+"F33.wireOp",EDGE,"E37");var subQ2=makeQuery(id+"F33.imprint","INTERSECT",VERTEX,{"disambiguationData":[OD(0.0)],"derivedFrom":[subQ1,subQ0]});Q5=makeQuery(id+"F33.imprint","IMPRINT",FACE,{"disambiguationData":[TD([[makeQuery(id+"F33.imprint","IMPRINT",EDGE,{"disambiguationData":[TD([[subQ2,-1.0]])],"derivedFrom":subQ1}),1.0]])]});}
            var Q6;
            {var subQ0=sQuery(id+"F33.wireOp",EDGE,"E42.right");var subQ1=sQuery(id+"F33.wireOp",EDGE,"E37");var subQ2=makeQuery(id+"F33.imprint","INTERSECT",VERTEX,{"disambiguationData":[OD(0.0)],"derivedFrom":[subQ1,subQ0]});Q6=makeQuery(id+"F33.imprint","IMPRINT",FACE,{"disambiguationData":[TD([[makeQuery(id+"F33.imprint","IMPRINT",EDGE,{"disambiguationData":[TD([[subQ2,-1.0]])],"derivedFrom":subQ1}),1.0]])]});}
            var Q7;
            {var subQ0=sQuery(id+"F33.wireOp",EDGE,"E42.right");var subQ1=sQuery(id+"F33.wireOp",EDGE,"E37");var subQ2=makeQuery(id+"F33.imprint","INTERSECT",VERTEX,{"disambiguationData":[OD(0.0)],"derivedFrom":[subQ1,subQ0]});Q7=makeQuery(id+"F33.imprint","IMPRINT",FACE,{"disambiguationData":[TD([[makeQuery(id+"F33.imprint","IMPRINT",EDGE,{"disambiguationData":[TD([[subQ2,1.0]])],"derivedFrom":subQ1}),1.0]])]});}
            extrude(context, id + "F35", {"entities" : qUnion([Q0, Q1, Q2, Q3, Q4, Q5, Q6, Q7]), "operationType" : NewBodyOperationType.ADD, "depth" : -26 * mm, "offsetDistance" : 25 * mm});
        }
        {
            var Q0;
            {var subQ5=sQuery(id+"F33.wireOp",EDGE,"E42.bottom");Q0=makeQuery(id+"F33.imprint","IMPRINT",FACE,{"disambiguationData":[TD([[makeQuery(id+"F33.imprint","IMPRINT",EDGE,{"derivedFrom":subQ5}),-1.0]])]});}
            var Q1;
            {var subQ5=sQuery(id+"F33.wireOp",EDGE,"E43.bottom");Q1=makeQuery(id+"F33.imprint","IMPRINT",FACE,{"disambiguationData":[TD([[makeQuery(id+"F33.imprint","IMPRINT",EDGE,{"derivedFrom":subQ5}),1.0]])]});}
            var Q2;
            {var subQ0=sQuery(id+"F33.wireOp",EDGE,"E43.right");var subQ1=sQuery(id+"F33.wireOp",EDGE,"E40");var subQ2=makeQuery(id+"F33.imprint","INTERSECT",VERTEX,{"disambiguationData":[OD(0.0)],"derivedFrom":[subQ1,subQ0]});Q2=makeQuery(id+"F33.imprint","IMPRINT",FACE,{"disambiguationData":[TD([[makeQuery(id+"F33.imprint","IMPRINT",EDGE,{"disambiguationData":[TD([[subQ2,1.0]])],"derivedFrom":subQ1}),1.0]])]});}
            var Q3;
            {var subQ0=sQuery(id+"F33.wireOp",EDGE,"E42.right");var subQ1=sQuery(id+"F33.wireOp",EDGE,"E40");var subQ2=makeQuery(id+"F33.imprint","INTERSECT",VERTEX,{"disambiguationData":[OD(0.0)],"derivedFrom":[subQ1,subQ0]});Q3=makeQuery(id+"F33.imprint","IMPRINT",FACE,{"disambiguationData":[TD([[makeQuery(id+"F33.imprint","IMPRINT",EDGE,{"disambiguationData":[TD([[subQ2,-1.0]])],"derivedFrom":subQ1}),1.0]])]});}
            var Q4;
            {var subQ0=sQuery(id+"F33.wireOp",EDGE,"E42.right");var subQ1=sQuery(id+"F33.wireOp",EDGE,"E37");var subQ2=makeQuery(id+"F33.imprint","INTERSECT",VERTEX,{"disambiguationData":[OD(0.0)],"derivedFrom":[subQ1,subQ0]});Q4=makeQuery(id+"F33.imprint","IMPRINT",FACE,{"disambiguationData":[TD([[makeQuery(id+"F33.imprint","IMPRINT",EDGE,{"disambiguationData":[TD([[subQ2,-1.0]])],"derivedFrom":subQ1}),-1.0]])]});}
            var Q5;
            {var subQ0=sQuery(id+"F33.wireOp",EDGE,"E43.right");var subQ1=sQuery(id+"F33.wireOp",EDGE,"E37");var subQ2=makeQuery(id+"F33.imprint","INTERSECT",VERTEX,{"disambiguationData":[OD(0.0)],"derivedFrom":[subQ1,subQ0]});Q5=makeQuery(id+"F33.imprint","IMPRINT",FACE,{"disambiguationData":[TD([[makeQuery(id+"F33.imprint","IMPRINT",EDGE,{"disambiguationData":[TD([[subQ2,1.0]])],"derivedFrom":subQ1}),-1.0]])]});}
            var Q6;
            {var subQ0=sQuery(id+"F33.wireOp",EDGE,"E43.right");var subQ1=sQuery(id+"F33.wireOp",EDGE,"E37");var subQ2=makeQuery(id+"F33.imprint","INTERSECT",VERTEX,{"disambiguationData":[OD(0.0)],"derivedFrom":[subQ1,subQ0]});Q6=makeQuery(id+"F33.imprint","IMPRINT",FACE,{"disambiguationData":[TD([[makeQuery(id+"F33.imprint","IMPRINT",EDGE,{"disambiguationData":[TD([[subQ2,1.0]])],"derivedFrom":subQ1}),1.0]])]});}
            var Q7;
            {var subQ0=sQuery(id+"F33.wireOp",EDGE,"E42.right");var subQ1=sQuery(id+"F33.wireOp",EDGE,"E37");var subQ2=makeQuery(id+"F33.imprint","INTERSECT",VERTEX,{"disambiguationData":[OD(0.0)],"derivedFrom":[subQ1,subQ0]});Q7=makeQuery(id+"F33.imprint","IMPRINT",FACE,{"disambiguationData":[TD([[makeQuery(id+"F33.imprint","IMPRINT",EDGE,{"disambiguationData":[TD([[subQ2,-1.0]])],"derivedFrom":subQ1}),1.0]])]});}
            extrude(context, id + "F36", {"entities" : qUnion([Q0, Q1, Q2, Q3, Q4, Q5, Q6, Q7]), "operationType" : NewBodyOperationType.REMOVE, "oppositeDirection" : true, "depth" : -4 * mm, "offsetDistance" : 25 * mm});
        }
        {
            var Q0;
            {var subQ0=sQuery(id+"F33.wireOp",EDGE,"E42.right");var subQ1=sQuery(id+"F33.wireOp",EDGE,"E40");var subQ2=makeQuery(id+"F33.imprint","INTERSECT",VERTEX,{"disambiguationData":[OD(0.0)],"derivedFrom":[subQ1,subQ0]});Q0=makeQuery(id+"F33.imprint","IMPRINT",FACE,{"disambiguationData":[TD([[makeQuery(id+"F33.imprint","IMPRINT",EDGE,{"disambiguationData":[TD([[subQ2,1.0]])],"derivedFrom":subQ1}),1.0]])]});}
            var Q1;
            {var subQ0=sQuery(id+"F33.wireOp",EDGE,"E42.right");var subQ1=sQuery(id+"F33.wireOp",EDGE,"E40");var subQ2=makeQuery(id+"F33.imprint","INTERSECT",VERTEX,{"disambiguationData":[OD(0.0)],"derivedFrom":[subQ1,subQ0]});Q1=makeQuery(id+"F33.imprint","IMPRINT",FACE,{"disambiguationData":[TD([[makeQuery(id+"F33.imprint","IMPRINT",EDGE,{"disambiguationData":[TD([[subQ2,-1.0]])],"derivedFrom":subQ1}),1.0]])]});}
            var Q2;
            {var subQ0=sQuery(id+"F33.wireOp",EDGE,"E43.right");var subQ1=sQuery(id+"F33.wireOp",EDGE,"E40");var subQ2=makeQuery(id+"F33.imprint","INTERSECT",VERTEX,{"disambiguationData":[OD(0.0)],"derivedFrom":[subQ1,subQ0]});Q2=makeQuery(id+"F33.imprint","IMPRINT",FACE,{"disambiguationData":[TD([[makeQuery(id+"F33.imprint","IMPRINT",EDGE,{"disambiguationData":[TD([[subQ2,1.0]])],"derivedFrom":subQ1}),1.0]])]});}
            var Q3;
            {var subQ0=sQuery(id+"F33.wireOp",EDGE,"E43.right");var subQ1=sQuery(id+"F33.wireOp",EDGE,"E40");var subQ2=makeQuery(id+"F33.imprint","INTERSECT",VERTEX,{"disambiguationData":[OD(0.0)],"derivedFrom":[subQ1,subQ0]});Q3=makeQuery(id+"F33.imprint","IMPRINT",FACE,{"disambiguationData":[TD([[makeQuery(id+"F33.imprint","IMPRINT",EDGE,{"disambiguationData":[TD([[subQ2,-1.0]])],"derivedFrom":subQ1}),1.0]])]});}
            var Q4;
            {var subQ0=sQuery(id+"F33.wireOp",EDGE,"E43.right");var subQ1=sQuery(id+"F33.wireOp",EDGE,"E37");var subQ2=makeQuery(id+"F33.imprint","INTERSECT",VERTEX,{"disambiguationData":[OD(0.0)],"derivedFrom":[subQ1,subQ0]});Q4=makeQuery(id+"F33.imprint","IMPRINT",FACE,{"disambiguationData":[TD([[makeQuery(id+"F33.imprint","IMPRINT",EDGE,{"disambiguationData":[TD([[subQ2,-1.0]])],"derivedFrom":subQ1}),1.0]])]});}
            var Q5;
            {var subQ0=sQuery(id+"F33.wireOp",EDGE,"E43.right");var subQ1=sQuery(id+"F33.wireOp",EDGE,"E37");var subQ2=makeQuery(id+"F33.imprint","INTERSECT",VERTEX,{"disambiguationData":[OD(0.0)],"derivedFrom":[subQ1,subQ0]});Q5=makeQuery(id+"F33.imprint","IMPRINT",FACE,{"disambiguationData":[TD([[makeQuery(id+"F33.imprint","IMPRINT",EDGE,{"disambiguationData":[TD([[subQ2,1.0]])],"derivedFrom":subQ1}),1.0]])]});}
            var Q6;
            {var subQ0=sQuery(id+"F33.wireOp",EDGE,"E42.right");var subQ1=sQuery(id+"F33.wireOp",EDGE,"E37");var subQ2=makeQuery(id+"F33.imprint","INTERSECT",VERTEX,{"disambiguationData":[OD(0.0)],"derivedFrom":[subQ1,subQ0]});Q6=makeQuery(id+"F33.imprint","IMPRINT",FACE,{"disambiguationData":[TD([[makeQuery(id+"F33.imprint","IMPRINT",EDGE,{"disambiguationData":[TD([[subQ2,-1.0]])],"derivedFrom":subQ1}),1.0]])]});}
            var Q7;
            {var subQ0=sQuery(id+"F33.wireOp",EDGE,"E42.right");var subQ1=sQuery(id+"F33.wireOp",EDGE,"E37");var subQ2=makeQuery(id+"F33.imprint","INTERSECT",VERTEX,{"disambiguationData":[OD(0.0)],"derivedFrom":[subQ1,subQ0]});Q7=makeQuery(id+"F33.imprint","IMPRINT",FACE,{"disambiguationData":[TD([[makeQuery(id+"F33.imprint","IMPRINT",EDGE,{"disambiguationData":[TD([[subQ2,1.0]])],"derivedFrom":subQ1}),1.0]])]});}
            extrude(context, id + "F37", {"entities" : qUnion([Q0, Q1, Q2, Q3, Q4, Q5, Q6, Q7]), "operationType" : NewBodyOperationType.ADD, "depth" : 11.5 * mm, "offsetDistance" : 25 * mm});
        }
        {
            var Q0;
            Q0=makeQuery(id+"F32.boolean.opBoolean","MERGE",FACE,{"derivedFrom":[makeQuery(id+"F32.opExtrude","CAP_FACE",FACE,{"disambiguationData":[OSD([sQuery(id+"F14.wireOp",EDGE,"E24.right"),sQuery(id+"F18.wireOp",EDGE,"E25.top"),sQuery(id+"F29.wireOp",EDGE,"E30.bottom"),sQuery(id+"F29.wireOp",EDGE,"E30.top"),sQuery(id+"F29.wireOp",EDGE,"E30.left"),sQuery(id+"F29.wireOp",EDGE,"E30.right")])],"isStart":true}),makeQuery(id+"F32.opExtrude","CAP_FACE",FACE,{"disambiguationData":[OSD([sQuery(id+"F23.wireOp",EDGE,"E27.bottom"),sQuery(id+"F23.wireOp",EDGE,"E27.right"),sQuery(id+"F25.wireOp",EDGE,"E28.top"),sQuery(id+"F25.wireOp",EDGE,"E28.right"),sQuery(id+"F27.wireOp",EDGE,"E29.bottom"),sQuery(id+"F27.wireOp",EDGE,"E29.top"),sQuery(id+"F27.wireOp",EDGE,"E29.left"),sQuery(id+"F31.wireOp",EDGE,"E31.bottom"),sQuery(id+"F31.wireOp",EDGE,"E31.top"),sQuery(id+"F31.wireOp",EDGE,"E31.right"),sQuery(id+"F31.wireOp",EDGE,"E32.right"),sQuery(id+"F31.wireOp",EDGE,"E33.top"),sQuery(id+"F31.wireOp",EDGE,"E33.right")])],"isStart":true})]});
            var sketch = newSketch(context, id + "F38", { "sketchPlane" : qUnion([Q0])});
            skLineSegment(sketch, "E44.bottom", {"start": v(6.5, -110.5) * mm, "end": v(46.5, -110.5) * mm});
            skLineSegment(sketch, "E44.top", {"start": v(6.5, -108.5) * mm, "end": v(46.5, -108.5) * mm});
            skLineSegment(sketch, "E44.left", {"start": v(6.5, -110.5) * mm, "end": v(6.5, -108.5) * mm});
            skLineSegment(sketch, "E44.right", {"start": v(46.5, -110.5) * mm, "end": v(46.5, -108.5) * mm});
            skSolve(sketch);
        }
        {
            var Q0;
            Q0 = qSketchRegion(id + "F38", true);
            extrude(context, id + "F39", {"entities" : qUnion([Q0]), "operationType" : NewBodyOperationType.ADD, "depth" : 18 * mm, "offsetDistance" : 25 * mm});
        }
    });
